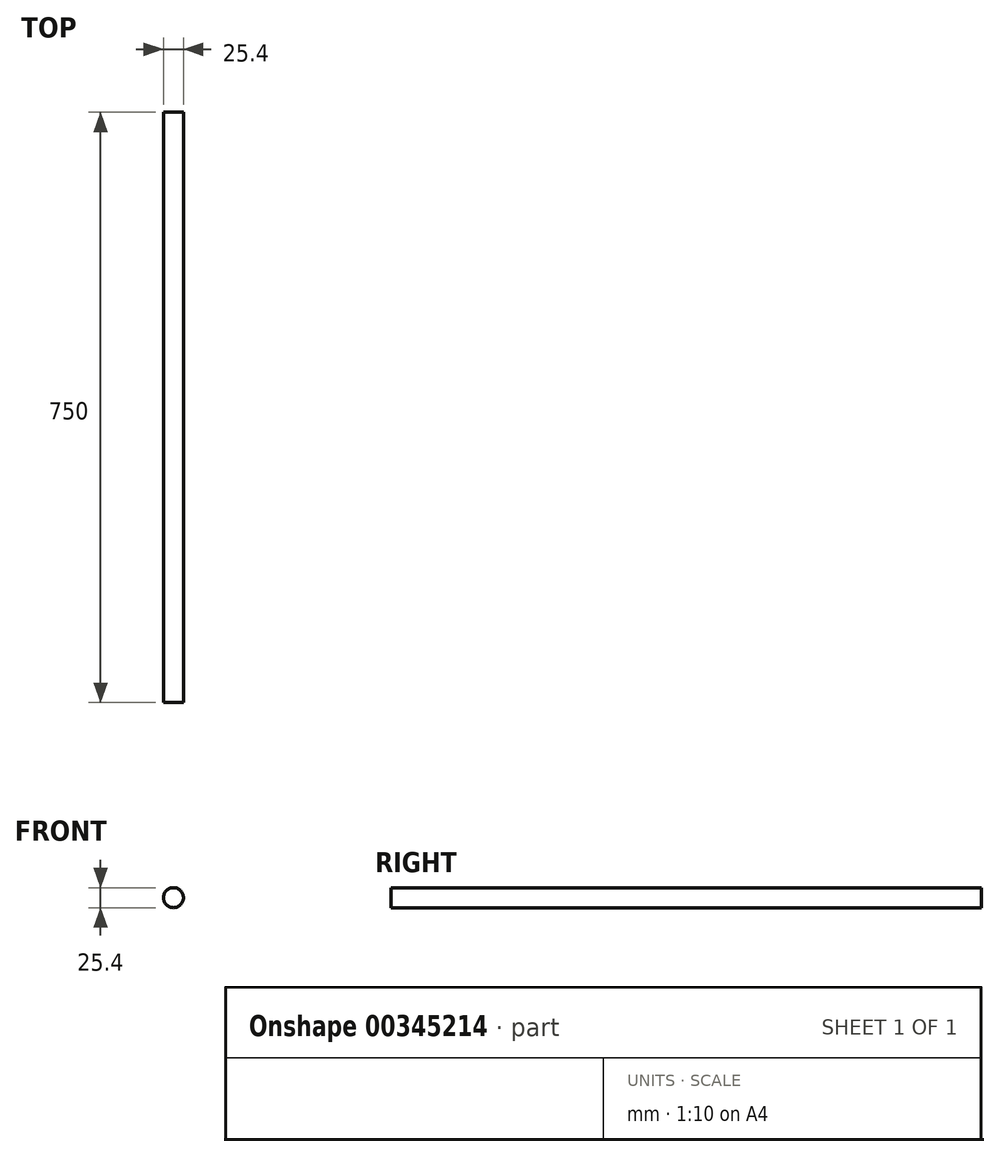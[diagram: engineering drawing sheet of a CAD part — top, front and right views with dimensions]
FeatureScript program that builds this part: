
annotation { "Feature Type Name" : "Feature", "Feature Type Description" : "" }
export const myFeature = defineFeature(function(context is Context, id is Id, definition is map)
    precondition{}
    {
        {
            var Q0;
            Q0=qCreatedBy(makeId("Front.planeOp"),FACE);
            var sketch = newSketch(context, id + "F0", { "sketchPlane" : qUnion([Q0])});
            skCircle(sketch, "E0", {"center": v(-16.84, 12.63) * mm, "radius": 12.7 * mm});
            skSolve(sketch);
        }
        {
            var Q0;
            Q0=makeQuery(id+"F0.imprint","IMPRINT",FACE,{"disambiguationData":[TD([[makeQuery(id+"F0.imprint","IMPRINT",EDGE,{"derivedFrom":sQuery(id+"F0.wireOp",EDGE,"E0")}),1.0]])]});
            extrude(context, id + "F1", {"entities" : qUnion([Q0]), "endBound" : BoundingType.SYMMETRIC, "depth" : 750 * mm});
        }
    });
